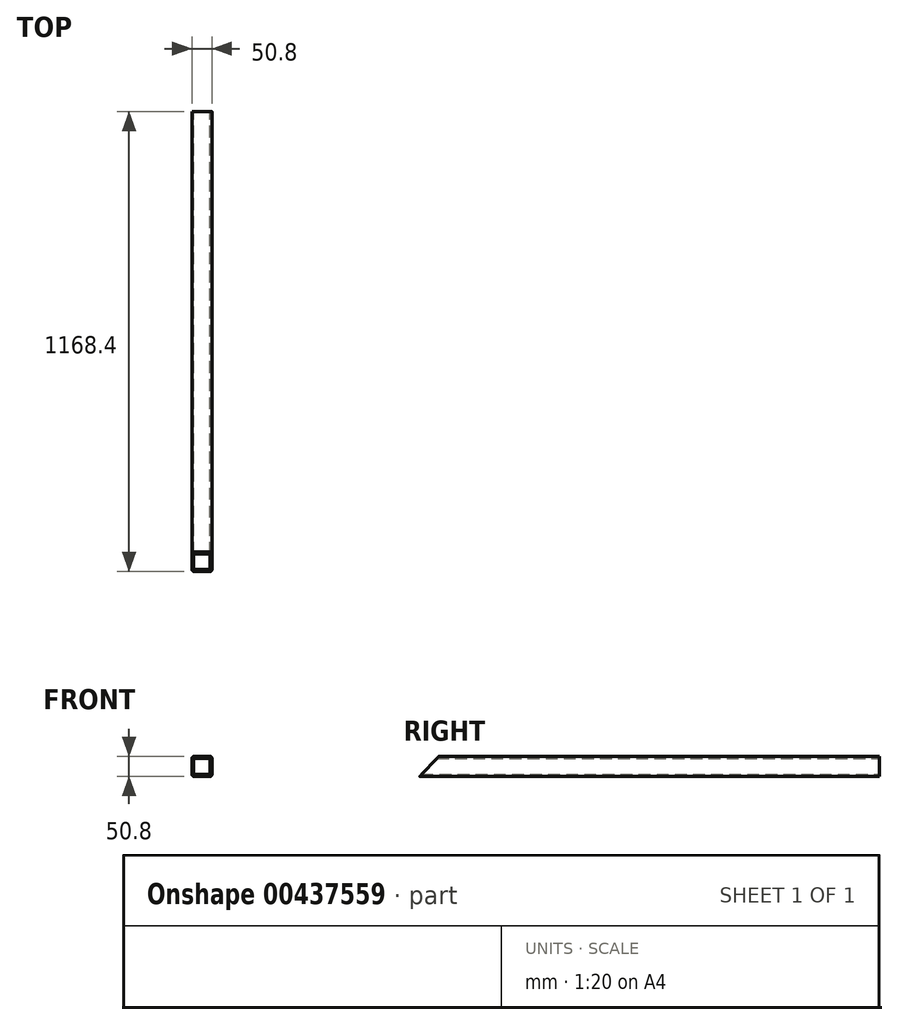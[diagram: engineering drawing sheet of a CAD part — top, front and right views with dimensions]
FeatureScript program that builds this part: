
annotation { "Feature Type Name" : "Feature", "Feature Type Description" : "" }
export const myFeature = defineFeature(function(context is Context, id is Id, definition is map)
    precondition{}
    {
        {
            var Q0;
            Q0=qCreatedBy(makeId("Front.planeOp"),FACE);
            var sketch = newSketch(context, id + "F0", { "sketchPlane" : qUnion([Q0])});
            skLineSegment(sketch, "E0.bottom", {"start": v(25.4, -25.4) * mm, "end": v(-25.4, -25.4) * mm});
            skLineSegment(sketch, "E0.top", {"start": v(25.4, 25.4) * mm, "end": v(-25.4, 25.4) * mm});
            skLineSegment(sketch, "E0.left", {"start": v(25.4, -25.4) * mm, "end": v(25.4, 25.4) * mm});
            skLineSegment(sketch, "E0.right", {"start": v(-25.4, -25.4) * mm, "end": v(-25.4, 25.4) * mm});
            skPoint(sketch, "E0.middle", {"position": v(0, 0) * mm});
            skLineSegment(sketch, "E1.bottom", {"start": v(20.64, -20.64) * mm, "end": v(-20.64, -20.64) * mm});
            skLineSegment(sketch, "E1.top", {"start": v(20.64, 20.64) * mm, "end": v(-20.64, 20.64) * mm});
            skLineSegment(sketch, "E1.left", {"start": v(20.64, -20.64) * mm, "end": v(20.64, 20.64) * mm});
            skLineSegment(sketch, "E1.right", {"start": v(-20.64, -20.64) * mm, "end": v(-20.64, 20.64) * mm});
            skSolve(sketch);
        }
        {
            var Q0;
            Q0 = qSketchRegion(id + "F0", true);
            extrude(context, id + "F1", {"entities" : qUnion([Q0]), "endBound" : BoundingType.SYMMETRIC, "depth" : 1168.4 * mm});
        }
        {
            var Q0;
            Q0=makeQuery(id+"F1.opExtrude","SWEPT_FACE",FACE,{"disambiguationData":[OSD([sQuery(id+"F0.wireOp",EDGE,"E0.left")])]});
            var sketch = newSketch(context, id + "F2", { "sketchPlane" : qUnion([Q0])});
            skPoint(sketch, "E2.0", {"position": v(-584.2, -25.4) * mm});
            skLineSegment(sketch, "E3", {"start": v(-584.2, -25.4) * mm, "end": v(-584.2, 25.4) * mm});
            skLineSegment(sketch, "E4", {"start": v(-584.2, -25.4) * mm, "end": v(-507.38, 54.15) * mm});
            skSolve(sketch);
        }
        {
            var Q0;
            Q0 = qSketchRegion(id + "F2", true);
            var Q1;
            {var subQ0=sQuery(id+"F2.wireOp",EDGE,"E3");Q1=makeQuery(id+"F2.imprint","IMPRINT",FACE,{"disambiguationData":[TD([[makeQuery(id+"F2.imprint","IMPRINT",EDGE,{"derivedFrom":subQ0}),-1.0]])]});}
            extrude(context, id + "F3", {"entities" : qUnion([Q0, Q1]), "operationType" : NewBodyOperationType.REMOVE, "oppositeDirection" : true, "depth" : 50.8 * mm});
        }
        {
            var Q0;
            Q0=makeQuery(id+"F1.opExtrude","SWEPT_EDGE",EDGE,{"disambiguationData":[OSD([sQuery(id+"F0.wireOp",EDGE,"E0.top"),sQuery(id+"F0.wireOp",EDGE,"E0.right")])]});
            var Q1;
            Q1=makeQuery(id+"F1.opExtrude","SWEPT_EDGE",EDGE,{"disambiguationData":[OSD([sQuery(id+"F0.wireOp",EDGE,"E0.top"),sQuery(id+"F0.wireOp",EDGE,"E0.left")])]});
            var Q2;
            Q2=makeQuery(id+"F1.opExtrude","SWEPT_EDGE",EDGE,{"disambiguationData":[OSD([sQuery(id+"F0.wireOp",EDGE,"E1.bottom"),sQuery(id+"F0.wireOp",EDGE,"E1.left")])]});
            var Q3;
            Q3=makeQuery(id+"F1.opExtrude","SWEPT_EDGE",EDGE,{"disambiguationData":[OSD([sQuery(id+"F0.wireOp",EDGE,"E1.bottom"),sQuery(id+"F0.wireOp",EDGE,"E1.right")])]});
            var Q4;
            Q4=makeQuery(id+"F1.opExtrude","SWEPT_EDGE",EDGE,{"disambiguationData":[OSD([sQuery(id+"F0.wireOp",EDGE,"E0.bottom"),sQuery(id+"F0.wireOp",EDGE,"E0.right")])]});
            var Q5;
            Q5=makeQuery(id+"F1.opExtrude","SWEPT_EDGE",EDGE,{"disambiguationData":[OSD([sQuery(id+"F0.wireOp",EDGE,"E0.bottom"),sQuery(id+"F0.wireOp",EDGE,"E0.left")])]});
            fillet(context, id + "F4", {"entities" : qUnion([Q0, Q1, Q2, Q3, Q4, Q5]), "radius" : 5.08 * mm, "tangentPropagation" : true, "allowEdgeOverflow" : false});
        }
    });
